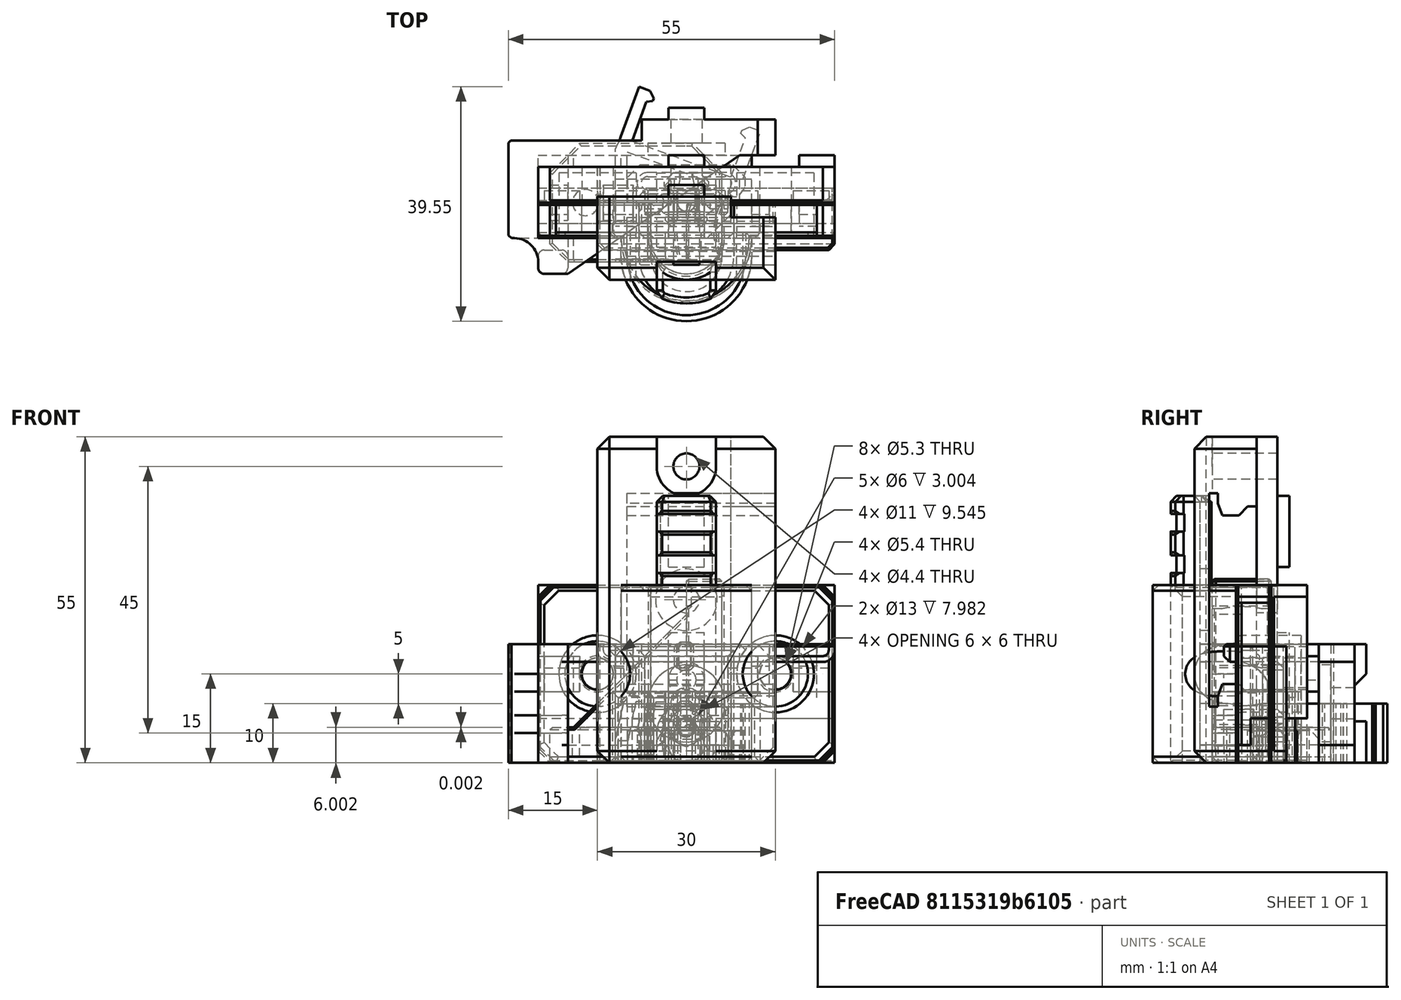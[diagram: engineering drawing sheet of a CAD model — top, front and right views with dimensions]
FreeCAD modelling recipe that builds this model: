
FCSTD DOCUMENT  (FreeCAD 0.18R16146 (Git))
Label: clip-mount
License: All rights reserved
LicenseURL: http://en.wikipedia.org/wiki/All_rights_reserved
objects: Part::Box×105, Part::Chamfer×66, Part::Cut×64, Part::MultiFuse×55, Part::Cylinder×49, Part::Feature×28, Part::Fillet×7
note: 374 computed .brp shape members not serialized (recipe doc carries the construction recipe); baked Part::Feature solids carry a one-line shape summary decoded from their .brp

FEATURE [Part::Box] Box  label="Cube"
  AttacherType = Attacher::AttachEngine3D
  Height = 6
  Length = 10
  Placement = pos=(-5,0,0) rot=(0,0,1;0rad)
  Width = 5
FEATURE [Part::Cylinder] Cylinder
  Angle = 360
  AttacherType = Attacher::AttachEngine3D
  Height = 2.5
  Placement = pos=(0,0.0010472,3) rot=(1,0,0;1.57045rad)
  Radius = 3
FEATURE [Part::Box] Box001  label="Cube001"
  AttacherType = Attacher::AttachEngine3D
  Height = 6
  Length = 10
  Placement = pos=(-5,-7.5,0) rot=(0,0,1;0rad)
  Width = 5
FEATURE [Part::Fillet] Fillet
  Base = -> Box
  Edges = 2 edges r=3: [Edge2,Edge8]
FEATURE [Part::MultiFuse] Fusion
  Shapes = -> [Fillet,Box001,Cylinder]
FEATURE [Part::Box] Box002  label="Cube002"
  AttacherType = Attacher::AttachEngine3D
  Height = 12
  Length = 2.25
  Placement = pos=(1.5,0,0) rot=(0,0,1;0rad)
  Width = 5
FEATURE [Part::Box] Box003  label="Cube003"
  AttacherType = Attacher::AttachEngine3D
  Height = 12
  Length = 2.25
  Placement = pos=(-3.75,0,0) rot=(0,0,1;0rad)
  Width = 5
FEATURE [Part::Box] Box004  label="Cube004"
  AttacherType = Attacher::AttachEngine3D
  Height = 12
  Length = 19
  Placement = pos=(-6.5,-6,0) rot=(0,0,1;0rad)
  Width = 6
FEATURE [Part::Box] Box005  label="Cube005"
  AttacherType = Attacher::AttachEngine3D
  Height = 12
  Length = 21
  Placement = pos=(7.5,-3.5,0) rot=(0,0,1;0rad)
  Width = 6
FEATURE [Part::Box] Box006  label="Cube006"
  AttacherType = Attacher::AttachEngine3D
  Height = 12
  Length = 1
  Placement = pos=(-4,0,0) rot=(0,0,1;0rad)
  Width = 2.7
FEATURE [Part::Box] Box007  label="Cube007"
  AttacherType = Attacher::AttachEngine3D
  Height = 12
  Length = 1
  Placement = pos=(3,0,0) rot=(0,0,1;0rad)
  Width = 2.7
FEATURE [Part::Cylinder] Cylinder001
  Angle = 360
  AttacherType = Attacher::AttachEngine3D
  Height = 12
  Radius = 1.5
FEATURE [Part::Box] Box008  label="Cube008"
  AttacherType = Attacher::AttachEngine3D
  Height = 10
  Length = 1
  Placement = pos=(-4,0,0) rot=(0,0,1;0rad)
  Width = 2.5
FEATURE [Part::Box] Box009  label="Cube009"
  AttacherType = Attacher::AttachEngine3D
  Height = 10
  Length = 1
  Placement = pos=(3,0,0) rot=(0,0,1;0rad)
  Width = 2.5
FEATURE [Part::Box] Box010  label="Cube010"
  AttacherType = Attacher::AttachEngine3D
  Height = 10
  Length = 1.5
  Placement = pos=(2,0,0) rot=(0,0,1;0rad)
  Width = 4
FEATURE [Part::Box] Box011  label="Cube011"
  AttacherType = Attacher::AttachEngine3D
  Height = 10
  Length = 1.5
  Placement = pos=(-3.5,0,0) rot=(0,0,1;0rad)
  Width = 4
FEATURE [Part::Cut] Cut004
  Base = -> Box011
  Tool = -> Box008
FEATURE [Part::Cut] Cut005
  Base = -> Box010
  Tool = -> Box009
FEATURE [Part::Chamfer] Chamfer004
  Base = -> Cut004
  Edges = 1 edges r=1: [Edge2]
FEATURE [Part::Chamfer] Chamfer005
  Base = -> Cut005
  Edges = 1 edges r=1: [Edge13]
FEATURE [Part::Box] Box012  label="Cube012"
  AttacherType = Attacher::AttachEngine3D
  Height = 10
  Length = 14
  Placement = pos=(-7,-2,0) rot=(0,0,1;0rad)
  Width = 2
FEATURE [Part::Box] Box014  label="Cube014"
  AttacherType = Attacher::AttachEngine3D
  Height = 6
  Length = 7
  Placement = pos=(3,-1,2) rot=(0,0,1;0rad)
  Width = 1
FEATURE [Part::Box] Box015  label="Cube015"
  AttacherType = Attacher::AttachEngine3D
  Height = 6
  Length = 7
  Placement = pos=(-10,-1,2) rot=(0,0,1;0rad)
  Width = 1
FEATURE [Part::Chamfer] Chamfer012
  Base = -> Box014
  Edges = 5 edges r=0.99: [Edge1,Edge2,Edge4,Edge9,Edge10]
FEATURE [Part::Chamfer] Chamfer013
  Base = -> Box015
  Edges = 4 edges r=0.99: [Edge5,Edge6,Edge8,Edge10]
FEATURE [Part::MultiFuse] Fusion004
  Shapes = -> [Chamfer013,Chamfer012]
FEATURE [Part::Cut] Cut010
  Base = -> Box012
  Tool = -> Fusion004
FEATURE [Part::MultiFuse] Fusion005
  Shapes = -> [Cut010,Chamfer005,Chamfer004]
FEATURE [Part::Chamfer] Chamfer014
  Base = -> Fusion005
  Edges = 4 edges r=1: [Edge1,Edge8,Edge15,Edge35]
FEATURE [Part::Chamfer] Chamfer015  label="cable-rail-cap-r1"
  Base = -> Chamfer014
  Edges = 8 edges r=0.4: [Edge4,Edge15,Edge19,Edge20,Edge21,Edge22,Edge23,Edge24]
FEATURE [Part::Cut] Cut
  Base = -> Box004
  Tool = -> Box005
FEATURE [Part::Cut] Cut011
  Base = -> Box003
  Tool = -> Box006
FEATURE [Part::Cut] Cut012
  Base = -> Box002
  Tool = -> Box007
FEATURE [Part::Chamfer] Chamfer
  Base = -> Cut012
  Edges = 1 edges r=1.5: [Edge13]
FEATURE [Part::Chamfer] Chamfer016
  Base = -> Cut011
  Edges = 1 edges r=1.5: [Edge2]
FEATURE [Part::Cut] Cut013
  Base = -> Cut
  Tool = -> Cylinder001
FEATURE [Part::MultiFuse] Fusion006
  Shapes = -> [Cut013,Chamfer016,Chamfer]
FEATURE [Part::Cylinder] Cylinder002
  Angle = 360
  AttacherType = Attacher::AttachEngine3D
  Height = 7
  Placement = pos=(0,-2.99791,6.00105) rot=(1,0,0;1.57045rad)
  Radius = 3
FEATURE [Part::Cylinder] Cylinder003
  Angle = 360
  AttacherType = Attacher::AttachEngine3D
  Height = 2
  Placement = pos=(0,1.00209,5.99965) rot=(1,0,0;1.57045rad)
  Radius = 1.65
FEATURE [Part::Cylinder] Cylinder004
  Angle = 360
  AttacherType = Attacher::AttachEngine3D
  Height = 5
  Placement = pos=(0,-0.997906,6.00035) rot=(1,0,0;1.57045rad)
  Radius = 1.5
FEATURE [Part::Box] Box016  label="Cube016"
  AttacherType = Attacher::AttachEngine3D
  Height = 12
  Length = 1
  Placement = pos=(-2,2,0) rot=(0,0,1;0rad)
  Width = 3
FEATURE [Part::Box] Box017  label="Cube017"
  AttacherType = Attacher::AttachEngine3D
  Height = 12
  Length = 1
  Placement = pos=(1,2,0) rot=(0,0,1;0rad)
  Width = 3
FEATURE [Part::Chamfer] Chamfer018
  Base = -> Box016
  Edges = 1 edges: [Edge5 r1=2.5 r2=0.5]
FEATURE [Part::Chamfer] Chamfer019
  Base = -> Box017
  Edges = 1 edges: [Edge1 r1=2.5 r2=0.5]
FEATURE [Part::MultiFuse] Fusion007
  Shapes = -> [Cylinder002,Cylinder004,Cylinder003]
FEATURE [Part::Cut] Cut014
  Base = -> Fusion006
  Tool = -> Fusion007
FEATURE [Part::Chamfer] Chamfer020
  Base = -> Cut014
  Edges = 2 edges: [Edge77 r1=1 r2=0.14,Edge86 r1=1 r2=0.14]
FEATURE [Part::MultiFuse] Fusion008
  Shapes = -> [Chamfer020,Chamfer019,Chamfer018]
FEATURE [Part::Cylinder] Cylinder005
  Angle = 360
  AttacherType = Attacher::AttachEngine3D
  Height = 10
  Placement = pos=(0,-0.0020944,6) rot=(-1,0,0;1.57045rad)
  Radius = 1.1
FEATURE [Part::Cut] Cut015
  Base = -> Fusion008
  Tool = -> Cylinder005
FEATURE [Part::Chamfer] Chamfer021
  Base = -> Cut015
  Edges = 4 edges r=1: [Edge69,Edge127,Edge128,Edge129]
FEATURE [Part::Chamfer] Chamfer022  label="plate-clip-r1"
  Base = -> Chamfer021
  Edges = 2 edges r=0.4: [Edge20,Edge22]
FEATURE [Part::Feature] Chamfer022001  label="plate-clip-r002"
  shape: bbox 19 x 11 x 12 mm, 70 faces (baked)
FEATURE [Part::Box] Box018  label="Cube018"
  AttacherType = Attacher::AttachEngine3D
  Height = 13
  Length = 22
  Placement = pos=(-8,-10,0) rot=(0,0,1;0rad)
  Width = 10
FEATURE [Part::Cut] Cut016
  Base = -> Chamfer022001
  Tool = -> Box018
FEATURE [Part::Box] Box019  label="Cube019"
  AttacherType = Attacher::AttachEngine3D
  Height = 19
  Length = 16
  Placement = pos=(-8,-6,0) rot=(0,0,1;0rad)
  Width = 6
FEATURE [Part::Box] Box020  label="Cube020"
  AttacherType = Attacher::AttachEngine3D
  Height = 19
  Length = 16
  Placement = pos=(-8,-3.5,12) rot=(0,0,1;0rad)
  Width = 3.5
FEATURE [Part::Cut] Cut017
  Base = -> Box019
  Tool = -> Box020
FEATURE [Part::Cylinder] Cylinder006
  Angle = 360
  AttacherType = Attacher::AttachEngine3D
  Height = 10
  Placement = pos=(0,-13.0021,5.99546) rot=(-1,0,0;1.57045rad)
  Radius = 3
FEATURE [Part::Cylinder] Cylinder007
  Angle = 360
  AttacherType = Attacher::AttachEngine3D
  Height = 16
  Placement = pos=(0,-13.0021,5.99546) rot=(-1,0,0;1.57045rad)
  Radius = 1.5
FEATURE [Part::MultiFuse] Fusion009
  Shapes = -> [Cylinder007,Cylinder006]
FEATURE [Part::Cut] Cut018
  Base = -> Cut017
  Tool = -> Fusion009
FEATURE [Part::MultiFuse] Fusion010
  Shapes = -> [Cut016,Cut018]
FEATURE [Part::Cylinder] Cylinder008
  Angle = 360
  AttacherType = Attacher::AttachEngine3D
  Height = 12
  Radius = 1.5
FEATURE [Part::Cut] Cut019
  Base = -> Fusion010
  Tool = -> Cylinder008
FEATURE [Part::Chamfer] Chamfer022002  label="side-clip-r1"
  Base = -> Cut019
  Edges = 4 edges r=1: [Edge6,Edge9,Edge25,Edge26]
FEATURE [Part::Box] Box021  label="Cube021"
  AttacherType = Attacher::AttachEngine3D
  Height = 12
  Length = 10
  Placement = pos=(3,-3.5,0) rot=(0,0,1;0rad)
  Width = 5
FEATURE [Part::Feature] Chamfer022003  label="plate-clip-r003"
  shape: bbox 19 x 11 x 12 mm, 70 faces (baked)
FEATURE [Part::Cut] Cut020  label="plate-clip-trim-r1"
  Base = -> Chamfer022003
  Tool = -> Box021
FEATURE [Part::Feature] Cut001  label="lcd-clip-origin"
  shape: bbox 19.81 x 6.72 x 6.352 mm, 53 faces (baked)
FEATURE [Part::Feature] Chamfer015001  label="cable-rail-cap-r002"
  Placement = pos=(0,0,0) rot=(0,0,1;3.14089rad)
  shape: bbox 14 x 6.006 x 10 mm, 58 faces (baked)
FEATURE [Part::Box] Box022  label="Cube022"
  AttacherType = Attacher::AttachEngine3D
  Height = 10
  Length = 16
  Placement = pos=(-9,0,0) rot=(0,0,1;0rad)
  Width = 10
FEATURE [Part::Cut] Cut021
  Base = -> Chamfer015001
  Tool = -> Box022
FEATURE [Part::Box] Box023  label="Cube023"
  AttacherType = Attacher::AttachEngine3D
  Height = 10
  Length = 22
  Placement = pos=(-10,-6,5.4) rot=(0,0,1;0rad)
  Width = 10
FEATURE [Part::Cut] Cut022
  Base = -> Cut021
  Tool = -> Box023
FEATURE [Part::Box] Box024  label="Cube024"
  AttacherType = Attacher::AttachEngine3D
  Height = 10
  Length = 10
  Placement = pos=(3,-1,0) rot=(0,0,1;0rad)
  Width = 10
FEATURE [Part::Cut] Cut023
  Base = -> Cut022
  Tool = -> Box024
FEATURE [Part::Feature] Chamfer022004  label="plate-clip-r004"
  shape: bbox 19 x 11 x 12 mm, 70 faces (baked)
FEATURE [Part::Feature] Chamfer022005  label="plate-clip-r005"
  Placement = pos=(-1e-15,0,12) rot=(0,1,0;3.14159rad)
  shape: bbox 19 x 11 x 12 mm, 70 faces (baked)
FEATURE [Part::MultiFuse] Fusion012
  Shapes = -> [Chamfer022005,Chamfer022004]
FEATURE [Part::Feature] Cut024001  label="Cut025"
  shape: bbox 30 x 5.5 x 20 mm, 11 faces (baked)
FEATURE [Part::Chamfer] Chamfer022006  label="din-spacer"
  Base = -> Cut024001
  Edges = 20 edges r=0.4: [Edge1,Edge2,Edge3,Edge4,Edge5,Edge6,Edge7,Edge9,Edge11,Edge12,Edge13,Edge14,Edge17,Edge18,Edge20,Edge22,Edge23,Edge25,Edge26,Edge27]
FEATURE [Part::Box] Box025  label="Cube025"
  AttacherType = Attacher::AttachEngine3D
  Height = 12
  Length = 6
  Placement = pos=(-3,1,10) rot=(0,0,1;0rad)
  Width = 2
FEATURE [Part::Box] Box026  label="Cube026"
  AttacherType = Attacher::AttachEngine3D
  Height = 55
  Length = 30
  Placement = pos=(-15,-13,0) rot=(0,0,1;0rad)
  Width = 14
FEATURE [Part::Box] Box027  label="Cube027"
  AttacherType = Attacher::AttachEngine3D
  Height = 36
  Length = 30
  Placement = pos=(-15,-10,-0.25) rot=(0,0,1;0rad)
  Width = 1.5
FEATURE [Part::Box] Box028  label="Cube028"
  AttacherType = Attacher::AttachEngine3D
  Height = 28.5
  Length = 30
  Placement = pos=(-15,-10,3.5) rot=(0,0,1;0rad)
  Width = 8
FEATURE [Part::Cylinder] Cylinder009
  Angle = 360
  AttacherType = Attacher::AttachEngine3D
  Height = 21
  Placement = pos=(0,-5,27.5) rot=(1,0,0;1.5708rad)
  Radius = 5.2
FEATURE [Part::Cylinder] Cylinder010
  Angle = 360
  AttacherType = Attacher::AttachEngine3D
  Height = 20
  Placement = pos=(0,3,5) rot=(1,0,0;1.5708rad)
  Radius = 5
FEATURE [Part::Cylinder] Cylinder011
  Angle = 360
  AttacherType = Attacher::AttachEngine3D
  Height = 20
  Placement = pos=(0,3,50) rot=(1,0,0;1.5708rad)
  Radius = 5
FEATURE [Part::Cylinder] Cylinder012
  Angle = 360
  AttacherType = Attacher::AttachEngine3D
  Height = 21
  Placement = pos=(0,3,27.5) rot=(1,0,0;1.5708rad)
  Radius = 2.2
FEATURE [Part::Cylinder] Cylinder013
  Angle = 360
  AttacherType = Attacher::AttachEngine3D
  Height = 20
  Placement = pos=(0,3,5) rot=(1,0,0;1.5708rad)
  Radius = 2.2
FEATURE [Part::Cylinder] Cylinder014
  Angle = 360
  AttacherType = Attacher::AttachEngine3D
  Height = 20
  Placement = pos=(0,3,50) rot=(1,0,0;1.5708rad)
  Radius = 2.2
FEATURE [Part::Box] Box029  label="Cube029"
  AttacherType = Attacher::AttachEngine3D
  Height = 12
  Length = 6
  Placement = pos=(-3,1,33) rot=(0,0,1;0rad)
  Width = 2
FEATURE [Part::MultiFuse] Fusion014
  Shapes = -> [Cylinder012,Cylinder014,Cylinder013]
FEATURE [Part::MultiFuse] Fusion016
  Placement = pos=(0,-13,0) rot=(0,0,1;0rad)
  Shapes = -> [Cylinder011,Cylinder010]
FEATURE [Part::Box] Box030  label="Cube030"
  AttacherType = Attacher::AttachEngine3D
  Height = 5
  Length = 10
  Placement = pos=(-5,-20,0) rot=(0,0,1;0rad)
  Width = 10
FEATURE [Part::Box] Box031  label="Cube031"
  AttacherType = Attacher::AttachEngine3D
  Height = 5
  Length = 10
  Placement = pos=(-5,-20,50) rot=(0,0,1;0rad)
  Width = 10
FEATURE [Part::MultiFuse] Fusion017
  Shapes = -> [Box031,Box030,Fusion016]
FEATURE [Part::MultiFuse] Fusion020
  Shapes = -> [Cylinder009,Fusion017,Fusion014]
FEATURE [Part::MultiFuse] Fusion021
  Shapes = -> [Box029,Box025]
FEATURE [Part::MultiFuse] Fusion022
  Shapes = -> [Box026,Fusion021]
FEATURE [Part::Cut] Cut024002
  Base = -> Fusion022
  Tool = -> Fusion020
FEATURE [Part::Box] Box032  label="Cube032"
  AttacherType = Attacher::AttachEngine3D
  Height = 55
  Length = 7.5
  Placement = pos=(7.5,-2.5,0) rot=(0,0,1;0rad)
  Width = 3.5
FEATURE [Part::Box] Box033  label="Cube033"
  AttacherType = Attacher::AttachEngine3D
  Height = 31.5
  Length = 30
  Placement = pos=(-15,-3.5,2) rot=(0,0,1;0rad)
  Width = 1.5
FEATURE [Part::MultiFuse] Fusion023
  Shapes = -> [Box033,Box028,Box027]
FEATURE [Part::Chamfer] Chamfer022007
  Base = -> Fusion023
  Edges = 2 edges r=1.49: [Edge6,Edge33]
FEATURE [Part::Chamfer] Chamfer022008
  Base = -> Chamfer022007
  Edges = 2 edges: [Edge26 r1=0.75 r2=2,Edge35 r1=0.75 r2=2]
  Placement = pos=(5,-0.5,9.75) rot=(0,0,1;0rad)
FEATURE [Part::Cut] Cut024003
  Base = -> Cut024002
  Tool = -> Chamfer022008
FEATURE [Part::Cut] Cut024004
  Base = -> Cut024003
  Tool = -> Box032
FEATURE [Part::Chamfer] Chamfer022009
  Base = -> Cut024004
  Edges = 9 edges r=2: [Edge1,Edge2,Edge4,Edge5,Edge9,Edge11,Edge15,Edge20,Edge40]
FEATURE [Part::Box] Box034  label="Cube034"
  AttacherType = Attacher::AttachEngine3D
  Height = 7
  Length = 6
  Placement = pos=(-3,0,0) rot=(0,0,1;0rad)
  Width = 2
FEATURE [Part::Box] Box036  label="Cube036"
  AttacherType = Attacher::AttachEngine3D
  Height = 20
  Length = 22.5
  Placement = pos=(-30,10.5,0) rot=(0,0,1;0rad)
  Width = 3.5
FEATURE [Part::Box] Box037  label="Cube037"
  AttacherType = Attacher::AttachEngine3D
  Height = 20
  Length = 5
  Placement = pos=(-25,-12,0) rot=(0,0,1;0rad)
  Width = 6
FEATURE [Part::Box] Box038  label="Cube038"
  AttacherType = Attacher::AttachEngine3D
  Height = 20
  Length = 15
  Placement = pos=(-30,-6,0) rot=(0,0,1;0rad)
  Width = 2.5
FEATURE [Part::Box] Box039  label="Cube039"
  AttacherType = Attacher::AttachEngine3D
  Height = 3
  Length = 30
  Placement = pos=(-21,-12,0) rot=(0,0,1;0rad)
  Width = 22
FEATURE [Part::Box] Box040  label="Cube040"
  AttacherType = Attacher::AttachEngine3D
  Height = 3
  Length = 21
  Placement = pos=(-21.5,-8,5) rot=(0,0,1;0rad)
  Width = 2
FEATURE [Part::Box] Box041  label="Cube041"
  AttacherType = Attacher::AttachEngine3D
  Height = 3
  Length = 21
  Placement = pos=(-21.5,-8,12) rot=(0,0,1;0rad)
  Width = 2
FEATURE [Part::Cylinder] Cylinder015
  Angle = 360
  AttacherType = Attacher::AttachEngine3D
  Height = 31
  Placement = pos=(0,2.2e-15,10) rot=(1,0,0;1.5708rad)
  Radius = 2.65
FEATURE [Part::Cylinder] Cylinder016
  Angle = 360
  AttacherType = Attacher::AttachEngine3D
  Height = 21
  Placement = pos=(0,-28,10) rot=(1,0,0;1.5708rad)
  Radius = 6.5
FEATURE [Part::Box] Box046  label="Cube046"
  AttacherType = Attacher::AttachEngine3D
  Height = 7
  Length = 6
  Placement = pos=(-2,0,13) rot=(0,0,1;0rad)
  Width = 2
FEATURE [Part::Chamfer] Chamfer022010005
  Base = -> Box046
  Edges = 1 edges r=1.99: [Edge11]
  Placement = pos=(-1,0,0) rot=(0,0,1;0rad)
FEATURE [Part::Box] Box047  label="Cube047"
  AttacherType = Attacher::AttachEngine3D
  Height = 30
  Length = 50
  Placement = pos=(-25,0,0) rot=(0,0,1;0rad)
  Width = 6
FEATURE [Part::Box] Box048  label="Cube048"
  AttacherType = Attacher::AttachEngine3D
  Height = 7.5
  Length = 50
  Placement = pos=(-25,2.5,0) rot=(0,0,1;0rad)
  Width = 3.5
FEATURE [Part::Box] Box049  label="Cube049"
  AttacherType = Attacher::AttachEngine3D
  Height = 6
  Length = 6
  Placement = pos=(-25,6,12) rot=(0,0,1;0rad)
  Width = 2
FEATURE [Part::Cylinder] Cylinder017
  Angle = 360
  AttacherType = Attacher::AttachEngine3D
  Height = 10
  Placement = pos=(15,5,15) rot=(1,0,0;1.5708rad)
  Radius = 6.5
FEATURE [Part::Cylinder] Cylinder018
  Angle = 360
  AttacherType = Attacher::AttachEngine3D
  Height = 10
  Placement = pos=(-15,5,15) rot=(1,0,0;1.5708rad)
  Radius = 6.5
FEATURE [Part::Cut] Cut024006003
  Base = -> Box047
  Tool = -> Box048
FEATURE [Part::Cylinder] Cylinder019
  Angle = 360
  AttacherType = Attacher::AttachEngine3D
  Height = 10
  Placement = pos=(15,5,15) rot=(1,0,0;1.5708rad)
  Radius = 2.65
FEATURE [Part::Cylinder] Cylinder020
  Angle = 360
  AttacherType = Attacher::AttachEngine3D
  Height = 10
  Placement = pos=(-15,5,15) rot=(1,0,0;1.5708rad)
  Radius = 2.65
FEATURE [Part::MultiFuse] Fusion028
  Placement = pos=(0,3,0) rot=(0,0,1;0rad)
  Shapes = -> [Cylinder020,Cylinder019]
FEATURE [Part::Box] Box050  label="Cube050"
  AttacherType = Attacher::AttachEngine3D
  Height = 6
  Length = 22
  Placement = pos=(-11,6,12) rot=(0,0,1;0rad)
  Width = 2
FEATURE [Part::Box] Box051  label="Cube051"
  AttacherType = Attacher::AttachEngine3D
  Height = 6
  Length = 6
  Placement = pos=(19,6,12) rot=(0,0,1;0rad)
  Width = 2
FEATURE [Part::Cut] Cut024006004
  Base = -> Cut024006003
  Tool = -> Fusion028
FEATURE [Part::Feature] Cut024006004001  label="Cut024006005"
  shape: bbox 50 x 6 x 30 mm, 10 faces (baked)
FEATURE [Part::Chamfer] Chamfer022010007
  Base = -> Cut024006004001
  Edges = 4 edges r=2: [Edge1,Edge5,Edge8,Edge18]
FEATURE [Part::Chamfer] Chamfer022010008
  Base = -> Chamfer022010007
  Edges = 10 edges r=0.4: [Edge4,Edge14,Edge18,Edge19,Edge20,Edge21,Edge22,Edge23,Edge24,Edge25]
FEATURE [Part::MultiFuse] Fusion029  label="extruder-cable-mount-base"
  Shapes = -> [Chamfer022010008,Box050,Box051,Box049]
FEATURE [Part::Cylinder] Cylinder021
  Angle = 360
  AttacherType = Attacher::AttachEngine3D
  Height = 30
  Placement = pos=(0,-6,0) rot=(0,0,1;0rad)
  Radius = 11
FEATURE [Part::Cylinder] Cylinder022
  Angle = 360
  AttacherType = Attacher::AttachEngine3D
  Height = 30
  Placement = pos=(0,-6,0) rot=(0,0,1;0rad)
  Radius = 6
FEATURE [Part::Box] Box053  label="Cube053"
  AttacherType = Attacher::AttachEngine3D
  Height = 30
  Length = 50
  Placement = pos=(-25,-6,0) rot=(0,0,1;0rad)
  Width = 6
FEATURE [Part::Cut] Cut024006004002
  Base = -> Cylinder021
  Tool = -> Cylinder022
FEATURE [Part::Box] Box054  label="Cube054"
  AttacherType = Attacher::AttachEngine3D
  Height = 30
  Length = 50
  Placement = pos=(-25,0,0) rot=(0,0,1;0rad)
  Width = 6
FEATURE [Part::Cut] Cut024006004003
  Base = -> Cut024006004002
  Tool = -> Box054
FEATURE [Part::Box] Box055  label="Cube055"
  AttacherType = Attacher::AttachEngine3D
  Height = 30
  Length = 12
  Placement = pos=(-6,-6,0) rot=(0,0,1;0rad)
  Width = 6
FEATURE [Part::Chamfer] Chamfer022010009
  Base = -> Box053
  Edges = 4 edges r=2: [Edge2,Edge4,Edge6,Edge8]
FEATURE [Part::Box] Box056  label="Cube056"
  AttacherType = Attacher::AttachEngine3D
  Height = 30
  Length = 12
  Placement = pos=(-6,-6,0) rot=(0,0,1;0rad)
  Width = 6
FEATURE [Part::Cut] Cut024006004004
  Base = -> Cut024006004003
  Tool = -> Box056
FEATURE [Part::Chamfer] Chamfer022010011
  Base = -> Cut024006004004
  Edges = 14 edges r=0.4: [Edge2,Edge4,Edge5,Edge7,Edge8,Edge9,Edge10,Edge11,Edge12,Edge14,Edge15,Edge16,Edge17,Edge18]
FEATURE [Part::Chamfer] Chamfer022010012
  Base = -> Chamfer022010011
  Edges = 2 edges r=0.4: [Edge14,Edge19]
FEATURE [Part::Cut] Cut024006004005
  Base = -> Chamfer022010009
  Tool = -> Box055
FEATURE [Part::Chamfer] Chamfer022010013
  Base = -> Cut024006004005
  Edges = 28 edges r=0.4: [Edge1,Edge4,Edge5,Edge6,Edge7,Edge8,Edge9,Edge11,Edge13,Edge14,Edge15,Edge16,Edge17,Edge18,Edge19,Edge20,Edge21,Edge22,Edge23,Edge24,Edge25,Edge27,Edge29,Edge31,Edge33,Edge34,Edge35,Edge36]
FEATURE [Part::MultiFuse] Fusion030
  Shapes = -> [Chamfer022010013,Chamfer022010012]
FEATURE [Part::Cylinder] Cylinder023
  Angle = 360
  AttacherType = Attacher::AttachEngine3D
  Height = 17
  Placement = pos=(15,-6,15) rot=(-1,0,0;1.5708rad)
  Radius = 6.5
FEATURE [Part::Cylinder] Cylinder024
  Angle = 360
  AttacherType = Attacher::AttachEngine3D
  Height = 17
  Placement = pos=(-15,-6,15) rot=(-1,0,0;1.5708rad)
  Radius = 6.5
FEATURE [Part::Cylinder] Cylinder025
  Angle = 360
  AttacherType = Attacher::AttachEngine3D
  Height = 10
  Placement = pos=(-15,-6,15) rot=(-1,0,0;1.5708rad)
  Radius = 2.65
FEATURE [Part::Cylinder] Cylinder026
  Angle = 360
  AttacherType = Attacher::AttachEngine3D
  Height = 10
  Placement = pos=(15,-6,15) rot=(-1,0,0;1.5708rad)
  Radius = 2.65
FEATURE [Part::MultiFuse] Fusion031
  Shapes = -> [Cylinder026,Cylinder025]
FEATURE [Part::Cut] Cut024006004006
  Base = -> Fusion030
  Tool = -> Fusion031
FEATURE [Part::MultiFuse] Fusion032
  Placement = pos=(0,-16,0) rot=(0,0,1;0rad)
  Shapes = -> [Cylinder024,Cylinder023]
FEATURE [Part::Cut] Cut024006004007
  Base = -> Cut024006004006
  Tool = -> Fusion032
FEATURE [Part::Cylinder] Cylinder027
  Angle = 360
  AttacherType = Attacher::AttachEngine3D
  Height = 16
  Placement = pos=(0,-6,29) rot=(0,0,1;0rad)
  Radius = 11
FEATURE [Part::Cylinder] Cylinder028
  Angle = 360
  AttacherType = Attacher::AttachEngine3D
  Height = 16
  Placement = pos=(0,-6,29) rot=(0,0,1;0rad)
  Radius = 6
FEATURE [Part::Cut] Cut024006004008
  Base = -> Cylinder027
  Tool = -> Cylinder028
FEATURE [Part::Box] Box057  label="Cube057"
  AttacherType = Attacher::AttachEngine3D
  Height = 20
  Length = 8
  Placement = pos=(-13,-17,28) rot=(0,0,1;0rad)
  Width = 10
FEATURE [Part::Box] Box058  label="Cube058"
  AttacherType = Attacher::AttachEngine3D
  Height = 20
  Length = 24
  Placement = pos=(-12,-8,28) rot=(0,0,1;0rad)
  Width = 13
FEATURE [Part::Cut] Cut024006004009
  Base = -> Cut024006004008
  Tool = -> Box058
FEATURE [Part::Box] Box059  label="Cube059"
  AttacherType = Attacher::AttachEngine3D
  Height = 20
  Length = 8
  Placement = pos=(5,-17,28) rot=(0,0,1;0rad)
  Width = 10
FEATURE [Part::Cylinder] Cylinder029
  Angle = 360
  AttacherType = Attacher::AttachEngine3D
  Height = 3
  Placement = pos=(0,-6,32) rot=(0,0,1;0rad)
  Radius = 12
FEATURE [Part::Cylinder] Cylinder030
  Angle = 360
  AttacherType = Attacher::AttachEngine3D
  Height = 3
  Placement = pos=(0,-6,32) rot=(0,0,1;0rad)
  Radius = 10
FEATURE [Part::Cut] Cut024006004012
  Base = -> Cylinder029
  Tool = -> Cylinder030
FEATURE [Part::Feature] Cut024006004012001  label="Cut024006004013"
  Placement = pos=(0,0,7) rot=(0,0,1;0rad)
  shape: bbox 24 x 24 x 3 mm, 4 faces (baked)
FEATURE [Part::Cut] Cut024006004012002
  Base = -> Cut024006004009
  Tool = -> Box057
FEATURE [Part::Cut] Cut024006004012003
  Base = -> Cut024006004012002
  Tool = -> Box059
FEATURE [Part::Chamfer] Chamfer022010014
  Base = -> Cut024006004012003
  Edges = 8 edges r=1: [Edge1,Edge2,Edge3,Edge5,Edge6,Edge8,Edge9,Edge10]
FEATURE [Part::Cut] Cut024006004012004
  Base = -> Chamfer022010014
  Tool = -> Cut024006004012001
FEATURE [Part::Cut] Cut024006004012005
  Base = -> Cut024006004012004
  Tool = -> Cut024006004012
FEATURE [Part::Feature] Cut024006004012005001  label="Cut024006004012006"
  shape: bbox 10.11 x 6.899 x 16 mm, 30 faces (baked)
FEATURE [Part::Chamfer] Chamfer022010015
  Base = -> Cut024006004012005001
  Edges = 4 edges r=0.5: [Edge2,Edge46,Edge52,Edge55]
FEATURE [Part::MultiFuse] Fusion033  label="extruder-cable-mount-rear"
  Shapes = -> [Chamfer022010015,Cut024006004007]
FEATURE [Part::Box] Box060  label="Cube060"
  AttacherType = Attacher::AttachEngine3D
  Height = 10
  Length = 21.8
  Width = 2
FEATURE [Part::Box] Box061  label="Cube061"
  AttacherType = Attacher::AttachEngine3D
  Height = 10
  Length = 2
  Width = 11
FEATURE [Part::Box] Box062  label="Cube062"
  AttacherType = Attacher::AttachEngine3D
  Height = 10
  Length = 2
  Placement = pos=(20,0,0) rot=(0,0,1;0rad)
  Width = 11
FEATURE [Part::Box] Box063  label="Cube063"
  AttacherType = Attacher::AttachEngine3D
  Height = 10
  Length = 3
  Placement = pos=(0,9,0) rot=(0,0,1;0rad)
  Width = 2
FEATURE [Part::Box] Box064  label="Cube064"
  AttacherType = Attacher::AttachEngine3D
  Height = 10
  Length = 3
  Placement = pos=(19,9,0) rot=(0,0,1;0rad)
  Width = 2
FEATURE [Part::Chamfer] Chamfer022010016
  Base = -> Box063
  Edges = 1 edges: [Edge5 r1=0.5 r2=1]
FEATURE [Part::Chamfer] Chamfer022010017
  Base = -> Box064
  Edges = 1 edges: [Edge1 r1=0.5 r2=1]
FEATURE [Part::Chamfer] Chamfer022010018
  Base = -> Chamfer022010016
  Edges = 1 edges r=1: [Edge3]
FEATURE [Part::Chamfer] Chamfer022010019
  Base = -> Chamfer022010017
  Edges = 1 edges r=1: [Edge3]
FEATURE [Part::MultiFuse] Fusion034
  Placement = pos=(-0.2,0,0) rot=(0,0,1;0rad)
  Shapes = -> [Box062,Chamfer022010019]
FEATURE [Part::MultiFuse] Fusion035
  Shapes = -> [Box061,Chamfer022010018]
FEATURE [Part::Box] Box065  label="Cube065"
  AttacherType = Attacher::AttachEngine3D
  Height = 20
  Length = 23
  Placement = pos=(-12,0,0) rot=(0,0,1;0rad)
  Width = 4
FEATURE [Part::Cylinder] Cylinder031
  Angle = 360
  AttacherType = Attacher::AttachEngine3D
  Height = 10
  Placement = pos=(0,12,14) rot=(1,0,0;1.5708rad)
  Radius = 3
FEATURE [Part::Box] Box066  label="Cube066"
  AttacherType = Attacher::AttachEngine3D
  Height = 20
  Length = 6
  Placement = pos=(-3,-1.5,0) rot=(0,0,1;0rad)
  Width = 1.5
FEATURE [Part::Cylinder] Cylinder032
  Angle = 360
  AttacherType = Attacher::AttachEngine3D
  Height = 10
  Placement = pos=(0,7,14) rot=(1,0,0;1.5708rad)
  Radius = 1.65
FEATURE [Part::Box] Box067  label="Cube067"
  AttacherType = Attacher::AttachEngine3D
  Height = 10
  Length = 2
  Placement = pos=(-12,3,0) rot=(0,0,1;0rad)
  Width = 7
FEATURE [Part::Chamfer] Chamfer022010021
  Base = -> Box067
  Edges = 1 edges: [Edge3 r1=1 r2=0.5]
FEATURE [Part::MultiFuse] Fusion038
  Placement = pos=(-11.7463,9.21193,0) rot=(0,0,-1;0.349066rad)
  Shapes = -> [Box060,Fusion034,Fusion035]
FEATURE [Part::Fillet] Fillet001
  Base = -> Box037
  Edges = 2 edges r=1: [Edge1,Edge5]
FEATURE [Part::MultiFuse] Fusion040
  Shapes = -> [Box038,Fillet001]
FEATURE [Part::Fillet] Fillet002
  Base = -> Fusion040
  Edges = 1 edges r=4: [Edge6]
FEATURE [Part::Chamfer] Chamfer022010022002
  Base = -> Fillet002
  Edges = 1 edges r=0.5: [Edge3]
FEATURE [Part::Box] Box042  label="Cube042"
  AttacherType = Attacher::AttachEngine3D
  Height = 3
  Length = 6.5
  Placement = pos=(-21.5,-12,12) rot=(0,0,1;0rad)
  Width = 6
FEATURE [Part::Box] Box043  label="Cube043"
  AttacherType = Attacher::AttachEngine3D
  Height = 3
  Length = 6.5
  Placement = pos=(-21.5,-12,5) rot=(0,0,1;0rad)
  Width = 6
FEATURE [Part::MultiFuse] Fusion041
  Placement = pos=(-10,0,0) rot=(0,0,1;0rad)
  Shapes = -> [Box043,Box042,Box040,Box041]
FEATURE [Part::Cut] Cut024006004012005004
  Base = -> Chamfer022010022002
  Tool = -> Fusion041
FEATURE [Part::Fillet] Fillet003
  Base = -> Cut024006004012005004
  Edges = 4 edges r=1: [Edge71,Edge75,Edge85,Edge111]
FEATURE [Part::Box] Box068  label="Cube068"
  AttacherType = Attacher::AttachEngine3D
  Height = 20
  Length = 40
  Placement = pos=(-15,0,0) rot=(0,0,1;0rad)
  Width = 6
FEATURE [Part::Box] Box069  label="Cube069"
  AttacherType = Attacher::AttachEngine3D
  Height = 3
  Length = 40
  Placement = pos=(-15,-8,17) rot=(0,0,1;0rad)
  Width = 8
FEATURE [Part::Cylinder] Cylinder033
  Angle = 360
  AttacherType = Attacher::AttachEngine3D
  Height = 10
  Placement = pos=(0,10,10) rot=(1,0,0;1.5708rad)
  Radius = 2.65
FEATURE [Part::Cylinder] Cylinder034
  Angle = 360
  AttacherType = Attacher::AttachEngine3D
  Height = 10
  Placement = pos=(0,2.2e-15,10) rot=(1,0,0;1.5708rad)
  Radius = 6.5
FEATURE [Part::MultiFuse] Fusion044
  Placement = pos=(0,2,0) rot=(0,0,1;0rad)
  Shapes = -> [Cylinder033,Cylinder034]
FEATURE [Part::MultiFuse] Fusion045
  Shapes = -> [Box069,Box068]
FEATURE [Part::Fillet] Fillet004
  Base = -> Fusion045
  Edges = 1 edges r=6: [Edge14]
FEATURE [Part::Fillet] Fillet005
  Base = -> Fillet004
  Edges = 6 edges r=2: [Edge1,Edge2,Edge9,Edge11,Edge14,Edge22]
FEATURE [Part::Box] Box070  label="Cube070"
  AttacherType = Attacher::AttachEngine3D
  Height = 23
  Length = 3
  Placement = pos=(19,-2,0) rot=(0,0,1;0rad)
  Width = 2
FEATURE [Part::Box] Box071  label="Cube071"
  AttacherType = Attacher::AttachEngine3D
  Height = 23
  Length = 3
  Placement = pos=(11,-2,0) rot=(0,0,1;0rad)
  Width = 2
FEATURE [Part::Box] Box072  label="Cube072"
  AttacherType = Attacher::AttachEngine3D
  Height = 23
  Length = 3
  Placement = pos=(-12,-2,0) rot=(0,0,1;0rad)
  Width = 2
FEATURE [Part::MultiFuse] Fusion046
  Shapes = -> [Box072,Box070,Box071]
FEATURE [Part::Chamfer] Chamfer022010022005
  Base = -> Fillet005
  Edges = 5 edges r=1: [Edge1,Edge7,Edge8,Edge9,Edge10]
FEATURE [Part::Chamfer] Chamfer022010022006
  Base = -> Chamfer022010022005
  Edges = 7 edges r=0.4: [Edge4,Edge12,Edge16,Edge17,Edge18,Edge21,Edge38]
FEATURE [Part::Cut] Cut024006004012005006
  Base = -> Chamfer022010022006
  Tool = -> Fusion044
FEATURE [Part::Cut] Cut024006004012005007
  Base = -> Cut024006004012005006
  Tool = -> Fusion046
FEATURE [Part::Chamfer] Chamfer022010022007
  Base = -> Cut024006004012005007
  Edges = 3 edges r=2: [Edge33,Edge37,Edge41]
FEATURE [Part::Box] Box073  label="Cube073"
  AttacherType = Attacher::AttachEngine3D
  Height = 6
  Length = 6
  Placement = pos=(-3,6,0) rot=(0,0,1;0rad)
  Width = 2
FEATURE [Part::Box] Box074  label="Cube074"
  AttacherType = Attacher::AttachEngine3D
  Height = 6
  Length = 6
  Placement = pos=(-3,6,14) rot=(0,0,1;0rad)
  Width = 2
FEATURE [Part::Chamfer] Chamfer022010022008
  Base = -> Box073
  Edges = 1 edges r=1.99: [Edge12]
FEATURE [Part::Fillet] Fillet006
  Base = -> Chamfer022010022007
  Edges = 3 edges r=1: [Edge69,Edge74,Edge76]
FEATURE [Part::MultiFuse] Fusion047
  Shapes = -> [Fillet006,Chamfer022010022008,Box074]
FEATURE [Part::Box] Box075  label="Cube075"
  AttacherType = Attacher::AttachEngine3D
  Height = 20
  Length = 18
  Placement = pos=(7.5,2.5,0) rot=(0,0,1;0rad)
  Width = 4
FEATURE [Part::Chamfer] Chamfer022010022009
  Base = -> Fusion047
  Edges = 11 edges r=0.4: [Edge64,Edge72,Edge90,Edge107,Edge130,Edge132,Edge133,Edge137,Edge138,Edge139,Edge140]
FEATURE [Part::Cut] Cut024006004012005008  label="power-cord"
  Base = -> Chamfer022010022009
  Tool = -> Box075
FEATURE [Part::Box] Box035  label="Cube035"
  AttacherType = Attacher::AttachEngine3D
  Height = 20
  Length = 45
  Placement = pos=(-30,-6,0) rot=(0,0,1;0rad)
  Width = 20
FEATURE [Part::MultiFuse] Fusion048
  Placement = pos=(0,14,0) rot=(0,0,1;0rad)
  Shapes = -> [Box034,Chamfer022010005]
FEATURE [Part::Chamfer] Chamfer022010022010
  Base = -> Box035
  Edges = 1 edges r=2: [Edge1]
FEATURE [Part::MultiFuse] Fusion050
  Placement = pos=(0,38,0) rot=(0,0,1;0rad)
  Shapes = -> [Cylinder016,Cylinder015]
FEATURE [Part::MultiFuse] Fusion051
  Shapes = -> [Chamfer022010022010,Fillet003]
FEATURE [Part::Box] Box076  label="Cube076"
  AttacherType = Attacher::AttachEngine3D
  Height = 20
  Length = 35
  Placement = pos=(-20,-10,0) rot=(0,0,1;0rad)
  Width = 18
FEATURE [Part::Cut] Cut024006004012005009
  Base = -> Fusion051
  Tool = -> Box076
FEATURE [Part::Chamfer] Chamfer022010022011
  Base = -> Box039
  Edges = 1 edges: [Edge5 r1=20 r2=29]
FEATURE [Part::Feature] Chamfer022010022011001  label="Chamfer022010022012"
  Placement = pos=(0,0,17) rot=(0,0,1;0rad)
  shape: bbox 30 x 22 x 3 mm, 7 faces (baked)
FEATURE [Part::Chamfer] Chamfer022010022011002
  Base = -> Cut024006004012005009
  Edges = 2 edges r=3: [Edge22,Edge44]
FEATURE [Part::MultiFuse] Fusion052
  Shapes = -> [Chamfer022010022011002,Chamfer022010022011001,Chamfer022010022011,Fusion048]
FEATURE [Part::Cut] Cut024006004012005010
  Base = -> Fusion052
  Tool = -> Box036
FEATURE [Part::Cut] Cut024006004012005011
  Base = -> Cut024006004012005010
  Tool = -> Fusion050
FEATURE [Part::Chamfer] Chamfer022010022011003
  Base = -> Cut024006004012005011
  Edges = 1 edges r=0.4: [Edge48]
FEATURE [Part::Cut] Cut024006004012005012
  Base = -> Box065
  Tool = -> Cylinder031
FEATURE [Part::Chamfer] Chamfer022010022011004
  Base = -> Cut024006004012005012
  Edges = 2 edges r=2: [Edge2,Edge9]
FEATURE [Part::MultiFuse] Fusion053
  Shapes = -> [Box066,Chamfer022010022011004]
FEATURE [Part::Cut] Cut024006004012005013
  Base = -> Fusion053
  Tool = -> Cylinder032
FEATURE [Part::MultiFuse] Fusion054  label="led-mount-m3"
  Shapes = -> [Cut024006004012005013,Fusion038,Chamfer022010021]
FEATURE [Part::Box] Box077  label="Cube077"
  AttacherType = Attacher::AttachEngine3D
  Height = 12
  Length = 3
  Placement = pos=(9.5,-10,0) rot=(0,0,1;0rad)
  Width = 6
FEATURE [Part::Box] Box078  label="Cube078"
  AttacherType = Attacher::AttachEngine3D
  Height = 6
  Length = 3
  Placement = pos=(9.5,-8,3) rot=(0,0,1;0rad)
  Width = 6
FEATURE [Part::Cut] Cut024006004012005014
  Base = -> Box077
  Tool = -> Box078
FEATURE [Part::Chamfer] Chamfer022010022011005
  Base = -> Cut024006004012005014
  Edges = 2 edges r=1: [Edge11,Edge23]
FEATURE [Part::Feature] Chamfer022010022011005001  label="Chamfer022010022011006"
  Placement = pos=(-16,0,0) rot=(0,0,1;0rad)
  shape: bbox 3 x 6 x 12 mm, 12 faces (baked)
FEATURE [Part::Feature] Chamfer022010022011005002  label="plate-clip-r006"
  shape: bbox 19 x 11 x 12 mm, 70 faces (baked)
FEATURE [Part::Feature] Chamfer022010022011005003  label="plate-clip-r007"
  shape: bbox 19 x 11 x 12 mm, 70 faces (baked)
FEATURE [Part::MultiFuse] Fusion055  label="cip-w-mounter-t1"
  Shapes = -> [Chamfer022010022011005002,Chamfer022010022011005001]
FEATURE [Part::MultiFuse] Fusion056  label="cip-w-mounter-t2"
  Shapes = -> [Chamfer022010022011005003,Chamfer022010022011005]
FEATURE [Part::Feature] Fusion055001  label="cip-w-mounter-t003"
  shape: bbox 19 x 15 x 12 mm, 84 faces (baked)
FEATURE [Part::Box] Box079  label="Cube079"
  AttacherType = Attacher::AttachEngine3D
  Height = 15
  Length = 10
  Placement = pos=(7.5,-9,0) rot=(0,0,1;0rad)
  Width = 10
FEATURE [Part::Box] Box080  label="Cube080"
  AttacherType = Attacher::AttachEngine3D
  Height = 15
  Length = 10
  Placement = pos=(7.5,-9,0) rot=(0,0,1;0rad)
  Width = 10
FEATURE [Part::Cut] Cut024006004012005015
  Base = -> Fusion055001
  Tool = -> Box080
FEATURE [Part::Chamfer] Chamfer022010022011005004
  Base = -> Box079
  Edges = 1 edges r=4: [Edge3]
  Placement = pos=(-4,-3,0) rot=(0,0,1;0rad)
FEATURE [Part::Cut] Cut024006004012005016  label="w-mounter-lite"
  Base = -> Cut024006004012005015
  Tool = -> Chamfer022010022011005004
FEATURE [Part::Feature] Chamfer022010022011005005
  Placement = pos=(-6.5,0,12.5) rot=(0,1,0;1.5708rad)
  shape: bbox 12 x 6 x 3 mm, 12 faces (baked)
FEATURE [Part::Feature] Chamfer022010022011005006  label="plate-clip-r008"
  shape: bbox 19 x 11 x 12 mm, 70 faces (baked)
FEATURE [Part::MultiFuse] Fusion055002  label="clip-sw-mounter"
  Shapes = -> [Chamfer022010022011005006,Chamfer022010022011005005]
FEATURE [Part::Box] Box081  label="Cube081"
  AttacherType = Attacher::AttachEngine3D
  Height = 8
  Length = 6
  Placement = pos=(-3,0,0) rot=(0,0,1;0rad)
  Width = 2
FEATURE [Part::Box] Box082  label="Cube082"
  AttacherType = Attacher::AttachEngine3D
  Height = 3
  Length = 6
  Placement = pos=(-3,-2,6) rot=(0,0,1;0rad)
  Width = 4
FEATURE [Part::Chamfer] Chamfer022010022011005007
  Base = -> Box082
  Edges = 1 edges r=2: [Edge9]
FEATURE [Part::Chamfer] Chamfer022010022011005008
  Base = -> Chamfer022010022011005007
  Edges = 1 edges r=1: [Edge11]
FEATURE [Part::Chamfer] Chamfer022010022011005009
  Base = -> Box081
  Edges = 1 edges r=1: [Edge11]
FEATURE [Part::MultiFuse] Fusion055003  label="LCD-w-mount"
  Shapes = -> [Chamfer022010022011005009,Cut023,Cut001,Chamfer022010022011005008]
FEATURE [Part::Feature] Chamfer022010022011005010  label="plate-clip-r009"
  shape: bbox 19 x 11 x 12 mm, 70 faces (baked)
FEATURE [Part::Box] Box083  label="Cube083"
  AttacherType = Attacher::AttachEngine3D
  Height = 12
  Length = 10
  Placement = pos=(-5,0,0) rot=(0,0,1;0rad)
  Width = 10
FEATURE [Part::Box] Box084  label="Cube084"
  AttacherType = Attacher::AttachEngine3D
  Height = 12
  Length = 6
  Placement = pos=(-3,-2,0) rot=(0,0,1;0rad)
  Width = 4
FEATURE [Part::Cut] Cut024006004012005017
  Base = -> Chamfer022010022011005010
  Tool = -> Box083
FEATURE [Part::Cylinder] Cylinder035
  Angle = 360
  AttacherType = Attacher::AttachEngine3D
  Height = 10
  Placement = pos=(0,3,6) rot=(1,0,0;1.5708rad)
  Radius = 1.65
FEATURE [Part::MultiFuse] Fusion055004
  Shapes = -> [Cut024006004012005017,Box084]
FEATURE [Part::Cut] Cut024006004012005018  label="panel-mount-std-7mm"
  Base = -> Fusion055004
  Tool = -> Cylinder035
FEATURE [Part::Feature] Cut020001  label="plate-clip-trim-r002"
  shape: bbox 19 x 11 x 12 mm, 70 faces (baked)
FEATURE [Part::Box] Box085  label="Cube085"
  AttacherType = Attacher::AttachEngine3D
  Height = 12
  Length = 10
  Placement = pos=(-5,0,0) rot=(0,0,1;0rad)
  Width = 10
FEATURE [Part::Box] Box086  label="Cube086"
  AttacherType = Attacher::AttachEngine3D
  Height = 12
  Length = 6
  Placement = pos=(-3,-2,0) rot=(0,0,1;0rad)
  Width = 4
FEATURE [Part::Cylinder] Cylinder036
  Angle = 360
  AttacherType = Attacher::AttachEngine3D
  Height = 10
  Placement = pos=(0,3,6) rot=(1,0,0;1.5708rad)
  Radius = 1.65
FEATURE [Part::Cut] Cut024006004012005019
  Base = -> Cut020001
  Tool = -> Box085
FEATURE [Part::Cylinder] Cylinder037
  Angle = 360
  AttacherType = Attacher::AttachEngine3D
  Height = 10
  Placement = pos=(0,3,6) rot=(1,0,0;1.5708rad)
  Radius = 1.65
FEATURE [Part::Box] Box087  label="Cube087"
  AttacherType = Attacher::AttachEngine3D
  Height = 12
  Length = 6
  Placement = pos=(3,-2,12) rot=(0,1,0;3.14159rad)
  Width = 4
FEATURE [Part::Box] Box088  label="Cube088"
  AttacherType = Attacher::AttachEngine3D
  Height = 12
  Length = 10
  Placement = pos=(-5,0,0) rot=(0,0,1;0rad)
  Width = 10
FEATURE [Part::Feature] Chamfer022002001  label="side-clip-r002"
  shape: bbox 16 x 11 x 19 mm, 68 faces (baked)
FEATURE [Part::Cut] Cut024006004012005021
  Base = -> Chamfer022002001
  Tool = -> Box088
FEATURE [Part::Box] Box089  label="Cube089"
  AttacherType = Attacher::AttachEngine3D
  Height = 19
  Length = 2.5
  Placement = pos=(-13,-4,0) rot=(0,0,1;0rad)
  Width = 4
FEATURE [Part::Box] Box090  label="Cube090"
  AttacherType = Attacher::AttachEngine3D
  Height = 12
  Length = 2
  Placement = pos=(3,-4,0) rot=(0,0,1;0rad)
  Width = 4
FEATURE [Part::MultiFuse] Fusion055005
  Shapes = -> [Cut024006004012005019,Box090,Box086]
FEATURE [Part::Cut] Cut024006004012005022  label="panel-mount-long-10mm"
  Base = -> Fusion055005
  Tool = -> Cylinder036
FEATURE [Part::Box] Box091  label="Cube091"
  AttacherType = Attacher::AttachEngine3D
  Height = 19
  Length = 6
  Placement = pos=(-13,-6,0) rot=(0,0,1;0rad)
  Width = 2.5
FEATURE [Part::Box] Box092  label="Cube092"
  AttacherType = Attacher::AttachEngine3D
  Height = 12
  Length = 6
  Placement = pos=(-7,-4,12) rot=(0,1,0;3.14159rad)
  Width = 4
FEATURE [Part::Chamfer] Chamfer022010022011005011
  Base = -> Box091
  Edges = 3 edges r=1: [Edge1,Edge9,Edge10]
FEATURE [Part::MultiFuse] Fusion055006
  Shapes = -> [Chamfer022010022011005011,Box092,Box089,Box087,Cut024006004012005021]
FEATURE [Part::Cut] Cut024006004012005023  label="panel-mount-top"
  Base = -> Fusion055006
  Tool = -> Cylinder037
FEATURE [Part::Box] Box100  label="Cube100"
  AttacherType = Attacher::AttachEngine3D
  Height = 30
  Length = 8
  Placement = pos=(0,-10,0) rot=(0,0,1;0rad)
  Width = 10
FEATURE [Part::Box] Box101  label="Cube101"
  AttacherType = Attacher::AttachEngine3D
  Height = 5
  Length = 24
  Placement = pos=(-23,-10,0) rot=(0,0,1;0rad)
  Width = 20
FEATURE [Part::Cylinder] Cylinder042
  Angle = 360
  AttacherType = Attacher::AttachEngine3D
  Height = 30
  Placement = pos=(15,-5,0) rot=(0,0,1;0rad)
  Radius = 10
FEATURE [Part::Cylinder] Cylinder043
  Angle = 360
  AttacherType = Attacher::AttachEngine3D
  Height = 4
  Placement = pos=(15,-5,0) rot=(0,0,1;0rad)
  Radius = 15
FEATURE [Part::Box] Box102  label="Cube102"
  AttacherType = Attacher::AttachEngine3D
  Height = 30
  Length = 8
  Placement = pos=(6,-10,0) rot=(0,0,1;0rad)
  Width = 10
FEATURE [Part::Cut] Cut024006004012005031
  Base = -> Box100
  Tool = -> Cylinder042
FEATURE [Part::Cut] Cut024006004012005032
  Base = -> Cut024006004012005031
  Tool = -> Box102
FEATURE [Part::Box] Box103  label="Cube103"
  AttacherType = Attacher::AttachEngine3D
  Height = 21
  Length = 21
  Placement = pos=(-20,-10,4) rot=(0,0,1;0rad)
  Width = 5
FEATURE [Part::Chamfer] Chamfer022010022011005012
  Base = -> Box103
  Edges = 1 edges r=20: [Edge2]
FEATURE [Part::Chamfer] Chamfer022010022011005015
  Base = -> Cut024006004012005032
  Edges = 8 edges r=0.4: [Edge1,Edge2,Edge3,Edge7,Edge8,Edge9,Edge10,Edge11]
FEATURE [Part::Box] Box104  label="Cube104"
  AttacherType = Attacher::AttachEngine3D
  Height = 5
  Length = 6
  Width = 10
FEATURE [Part::Chamfer] Chamfer022010022011005016
  Base = -> Box104
  Edges = 1 edges r=5: [Edge7]
FEATURE [Part::Chamfer] Chamfer022010022011005017
  Base = -> Chamfer022010022011005016
  Edges = 3 edges r=0.4: [Edge1,Edge5,Edge6]
FEATURE [Part::Chamfer] Chamfer022010022011005014
  Base = -> Chamfer022010022011005012
  Edges = 1 edges r=0.4: [Edge6]
  Placement = pos=(1,0,0) rot=(0,0,1;0rad)
FEATURE [Part::Cylinder] Cylinder044
  Angle = 360
  AttacherType = Attacher::AttachEngine3D
  Height = 4
  Placement = pos=(15,-5,0) rot=(0,0,1;0rad)
  Radius = 17
FEATURE [Part::Cut] Cut024006004012005033
  Base = -> Cylinder044
  Placement = pos=(0,0,5) rot=(0,0,1;0rad)
  Tool = -> Cylinder043
FEATURE [Part::Feature] Cut024006004012005033001  label="Cut024006004012005034"
  Placement = pos=(0,0,25) rot=(0,0,1;0rad)
  shape: bbox 34 x 34 x 4 mm, 4 faces (baked)
FEATURE [Part::Feature] Cut024006004012005033002  label="Cut024006004012005035"
  Placement = pos=(0,0,15) rot=(0,0,1;0rad)
  shape: bbox 34 x 34 x 4 mm, 4 faces (baked)
FEATURE [Part::MultiFuse] Fusion055010
  Shapes = -> [Cut024006004012005033,Cut024006004012005033002,Cut024006004012005033001]
FEATURE [Part::Chamfer] Chamfer022010022011005020
  Base = -> Fusion055010
  Edges = 12 edges r=0.4: [Edge1,Edge3,Edge4,Edge5,Edge7,Edge9,Edge10,Edge11,Edge13,Edge15,Edge16,Edge17]
FEATURE [Part::Cylinder] Cylinder045
  Angle = 360
  AttacherType = Attacher::AttachEngine3D
  Height = 10
  Radius = 2.2
FEATURE [Part::Cylinder] Cylinder046
  Angle = 360
  AttacherType = Attacher::AttachEngine3D
  Height = 4
  Placement = pos=(0,0,6) rot=(0,0,1;0rad)
  Radius = 5
FEATURE [Part::MultiFuse] Fusion055011
  Placement = pos=(-6,0,0) rot=(0,0,1;0rad)
  Shapes = -> [Cylinder046,Cylinder045]
FEATURE [Part::Feature] Fusion055011001  label="Fusion055012"
  Placement = pos=(-17,0,0) rot=(0,0,1;0rad)
  shape: bbox 10 x 10 x 10 mm, 6 faces (baked)
FEATURE [Part::Chamfer] Chamfer022010022011005021
  Base = -> Box101
  Edges = 1 edges r=5: [Edge3]
FEATURE [Part::Chamfer] Chamfer022010022011005022
  Base = -> Chamfer022010022011005021
  Edges = 1 edges r=3: [Edge3]
FEATURE [Part::Chamfer] Chamfer022010022011005023
  Base = -> Chamfer022010022011005022
  Edges = 5 edges r=0.4: [Edge1,Edge5,Edge6,Edge7,Edge8]
FEATURE [Part::MultiFuse] Fusion055011002
  Shapes = -> [Chamfer022010022011005023,Chamfer022010022011005017,Chamfer022010022011005014,Chamfer022010022011005015]
FEATURE [Part::Cut] Cut024006004012005033003
  Base = -> Fusion055011002
  Tool = -> Chamfer022010022011005020
FEATURE [Part::MultiFuse] Fusion055011003
  Shapes = -> [Fusion055011001,Fusion055011]
FEATURE [Part::Cut] Cut024006004012005033004
  Base = -> Cut024006004012005033003
  Placement = pos=(0,0,1) rot=(0,0,1;0rad)
  Tool = -> Fusion055011003
FEATURE [Part::Box] Box105  label="Cube105"
  AttacherType = Attacher::AttachEngine3D
  Height = 2
  Length = 3
  Placement = pos=(-23,-3,-2) rot=(0,0,1;0rad)
  Width = 6
FEATURE [Part::Box] Box106  label="Cube106"
  AttacherType = Attacher::AttachEngine3D
  Height = 2
  Length = 5
  Placement = pos=(-14,-3,-2) rot=(0,0,1;0rad)
  Width = 6
FEATURE [Part::Box] Box107  label="Cube107"
  AttacherType = Attacher::AttachEngine3D
  Height = 2
  Length = 8
  Placement = pos=(-3,-3,-2) rot=(0,0,1;0rad)
  Width = 6
FEATURE [Part::Feature] hevort_lite_door_handle_1_001001_solid  label="hevort-logo"
  Placement = pos=(-65,-23.5,2) rot=(0,0,1;0rad)
  shape: bbox 20 x 23 x 20 mm, 66 faces (baked)
FEATURE [Part::Box] Box108  label="Cube108"
  AttacherType = Attacher::AttachEngine3D
  Height = 7.5
  Length = 50
  Placement = pos=(-25,-3.5,0) rot=(0,0,1;0rad)
  Width = 3.5
FEATURE [Part::Box] Box109  label="Cube109"
  AttacherType = Attacher::AttachEngine3D
  Height = 6
  Length = 6
  Placement = pos=(-24,-1,12) rot=(0,0,1;0rad)
  Width = 3
FEATURE [Part::Box] Box110  label="Cube110"
  AttacherType = Attacher::AttachEngine3D
  Height = 6
  Length = 5
  Placement = pos=(-12,-1,12) rot=(0,0,1;0rad)
  Width = 3
FEATURE [Part::Chamfer] Chamfer022010022011005026
  Base = -> Box110
  Edges = 1 edges r=2: [Edge12]
FEATURE [Part::Chamfer] Chamfer022010022011005027
  Base = -> Box109
  Edges = 1 edges r=2: [Edge12]
FEATURE [Part::Feature] Chamfer022010022011005026001  label="Chamfer022010022011005028"
  Placement = pos=(19,0,0) rot=(0,0,1;0rad)
  shape: bbox 5 x 3 x 6 mm, 7 faces (baked)
FEATURE [Part::Feature] Chamfer022010022011005027001  label="Chamfer022010022011005029"
  Placement = pos=(42,0,0) rot=(0,0,1;0rad)
  shape: bbox 6 x 3 x 6 mm, 7 faces (baked)
FEATURE [Part::MultiFuse] Fusion055011005003
  Placement = pos=(0,0,2) rot=(0,0,1;0rad)
  Shapes = -> [Box106,Box107,Box105]
FEATURE [Part::Chamfer] Chamfer022010022011005027002
  Base = -> Fusion055011005003
  Edges = 3 edges r=1: [Edge9,Edge21,Edge33]
FEATURE [Part::MultiFuse] Fusion055011005004
  Shapes = -> [Chamfer022010022011005027002,Cut024006004012005033004]
FEATURE [Part::Cut] Cut024006004012005033007
  Base = -> Fusion055011005004
  Tool = -> hevort_lite_door_handle_1_001001_solid
FEATURE [Part::Feature] Cut024006004012005033007001  label="Cut024006004012005033008"
  shape: bbox 29 x 20.13 x 31 mm, 149 faces (baked)
FEATURE [Part::Chamfer] Chamfer022010022011005027003  label="extruder-cable-top-mounter"
  Base = -> Cut024006004012005033007001
  Edges = 16 edges r=0.4: [Edge142,Edge145,Edge147,Edge149,Edge151,Edge153,Edge156,Edge158,Edge160,Edge166,Edge168,Edge175,Edge208,Edge290,Edge291,Edge292]
FEATURE [Part::Cylinder] Cylinder047
  Angle = 360
  AttacherType = Attacher::AttachEngine3D
  Height = 10
  Placement = pos=(-15,-6,15) rot=(1,0,0;1.5708rad)
  Radius = 5.5
FEATURE [Part::Cylinder] Cylinder048
  Angle = 360
  AttacherType = Attacher::AttachEngine3D
  Height = 10
  Placement = pos=(15,-6,15) rot=(1,0,0;1.5708rad)
  Radius = 5.5
FEATURE [Part::MultiFuse] Fusion055011005005
  Placement = pos=(0,1,0) rot=(0,0,1;0rad)
  Shapes = -> [Cylinder048,Cylinder047]
FEATURE [Part::Cylinder] Cylinder049
  Angle = 360
  AttacherType = Attacher::AttachEngine3D
  Height = 30
  Placement = pos=(0,-6,0) rot=(0,0,1;0rad)
  Radius = 6
FEATURE [Part::Cylinder] Cylinder050
  Angle = 360
  AttacherType = Attacher::AttachEngine3D
  Height = 30
  Placement = pos=(0,-6,0) rot=(0,0,1;0rad)
  Radius = 11
FEATURE [Part::Cut] Cut024006004012005033007002
  Base = -> Cylinder050
  Placement = pos=(0,-3,0) rot=(0,0,1;0rad)
  Tool = -> Cylinder049
FEATURE [Part::Box] Box111  label="Cube111"
  AttacherType = Attacher::AttachEngine3D
  Height = 30
  Length = 36
  Placement = pos=(-17,-9,0) rot=(0,0,1;0rad)
  Width = 15
FEATURE [Part::Cut] Cut024006004012005033007003
  Base = -> Cut024006004012005033007002
  Tool = -> Box111
FEATURE [Part::Box] Box112  label="Cube112"
  AttacherType = Attacher::AttachEngine3D
  Height = 30
  Length = 5
  Placement = pos=(-11,-9,0) rot=(0,0,1;0rad)
  Width = 6
FEATURE [Part::Box] Box113  label="Cube113"
  AttacherType = Attacher::AttachEngine3D
  Height = 30
  Length = 5
  Placement = pos=(6,-9,0) rot=(0,0,1;0rad)
  Width = 6
FEATURE [Part::Box] Box114  label="Cube114"
  AttacherType = Attacher::AttachEngine3D
  Height = 30
  Length = 50
  Placement = pos=(-25,-6,0) rot=(0,0,1;0rad)
  Width = 6
FEATURE [Part::Box] Box115  label="Cube115"
  AttacherType = Attacher::AttachEngine3D
  Height = 30
  Length = 12
  Placement = pos=(-6,-6,0) rot=(0,0,1;0rad)
  Width = 6
FEATURE [Part::MultiFuse] Fusion055011005007
  Shapes = -> [Chamfer022010022011005027,Chamfer022010022011005026,Chamfer022010022011005026001,Chamfer022010022011005027001]
FEATURE [Part::Cylinder] Cylinder051
  Angle = 360
  AttacherType = Attacher::AttachEngine3D
  Height = 10
  Placement = pos=(-15,3.3e-15,15) rot=(1,0,0;1.5708rad)
  Radius = 2.7
FEATURE [Part::Cylinder] Cylinder052
  Angle = 360
  AttacherType = Attacher::AttachEngine3D
  Height = 10
  Placement = pos=(15,3e-15,15) rot=(1,0,0;1.5708rad)
  Radius = 2.7
FEATURE [Part::MultiFuse] Fusion055011005009
  Placement = pos=(0,2,0) rot=(0,0,1;0rad)
  Shapes = -> [Cylinder051,Cylinder052]
FEATURE [Part::MultiFuse] Fusion055011005010
  Shapes = -> [Box114,Cut024006004012005033007003,Box112,Box113,Fusion055011005007]
FEATURE [Part::Cut] Cut024006004012005033007004
  Base = -> Fusion055011005010
  Tool = -> Box115
FEATURE [Part::Cut] Cut024006004012005033007005
  Base = -> Cut024006004012005033007004
  Tool = -> Box108
FEATURE [Part::MultiFuse] Fusion055011005011
  Shapes = -> [Fusion055011005009,Fusion055011005005]
FEATURE [Part::Cut] Cut024006004012005033007006
  Base = -> Cut024006004012005033007005
  Tool = -> Fusion055011005011
FEATURE [Part::Chamfer] Chamfer022010022011005027004
  Base = -> Cut024006004012005033007006
  Edges = 4 edges r=3: [Edge1,Edge5,Edge110,Edge112]
FEATURE [Part::Feature] Chamfer022010022011005027004001  label="Chamfer022010022011005027005"
  shape: bbox 50 x 22 x 30 mm, 50 faces (baked)
FEATURE [Part::Chamfer] Chamfer022010022011005027004002
  Base = -> Chamfer022010022011005027004001
  Edges = 3 edges r=2: [Edge125,Edge126,Edge127]
FEATURE [Part::Chamfer] Chamfer022010022011005027004003
  Base = -> Chamfer022010022011005027004002
  Edges = 3 edges r=2: [Edge32,Edge100,Edge102]
FEATURE [Part::Chamfer] Chamfer022010022011005027004004
  Base = -> Chamfer022010022011005027004003
  Edges = 15 edges r=1: [Edge44,Edge46,Edge48,Edge50,Edge51,Edge53,Edge57,Edge59,Edge60,Edge61,Edge64,Edge65,Edge113,Edge117,Edge119]
